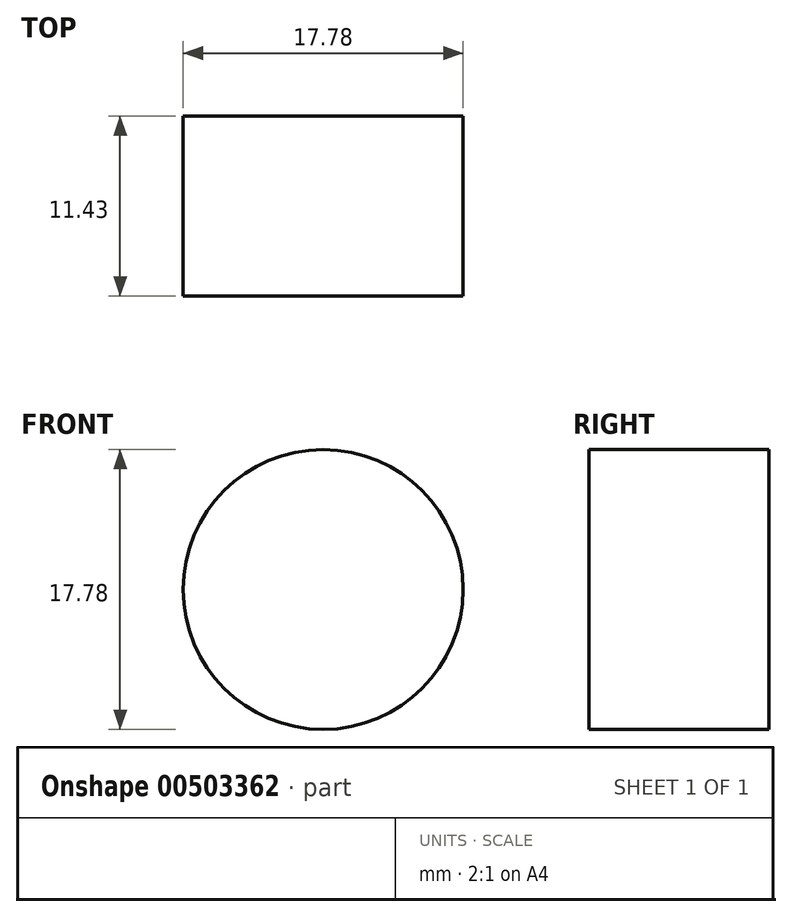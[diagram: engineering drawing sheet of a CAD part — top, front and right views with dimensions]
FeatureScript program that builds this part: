
annotation { "Feature Type Name" : "Feature", "Feature Type Description" : "" }
export const myFeature = defineFeature(function(context is Context, id is Id, definition is map)
    precondition{}
    {
        {
            var Q0;
            Q0=qCreatedBy(makeId("Front.planeOp"),FACE);
            var sketch = newSketch(context, id + "F0", { "sketchPlane" : qUnion([Q0])});
            skCircle(sketch, "E0", {"center": v(0, 0) * mm, "radius": 8.9 * mm});
            skSolve(sketch);
        }
        {
            var Q0;
            Q0=makeQuery(id+"F0.imprint","IMPRINT",FACE,{"disambiguationData":[TD([[makeQuery(id+"F0.imprint","IMPRINT",EDGE,{"derivedFrom":sQuery(id+"F0.wireOp",EDGE,"E0")}),1.0]])]});
            extrude(context, id + "F1", {"entities" : qUnion([Q0]), "depth" : 11.43 * mm});
        }
    });
